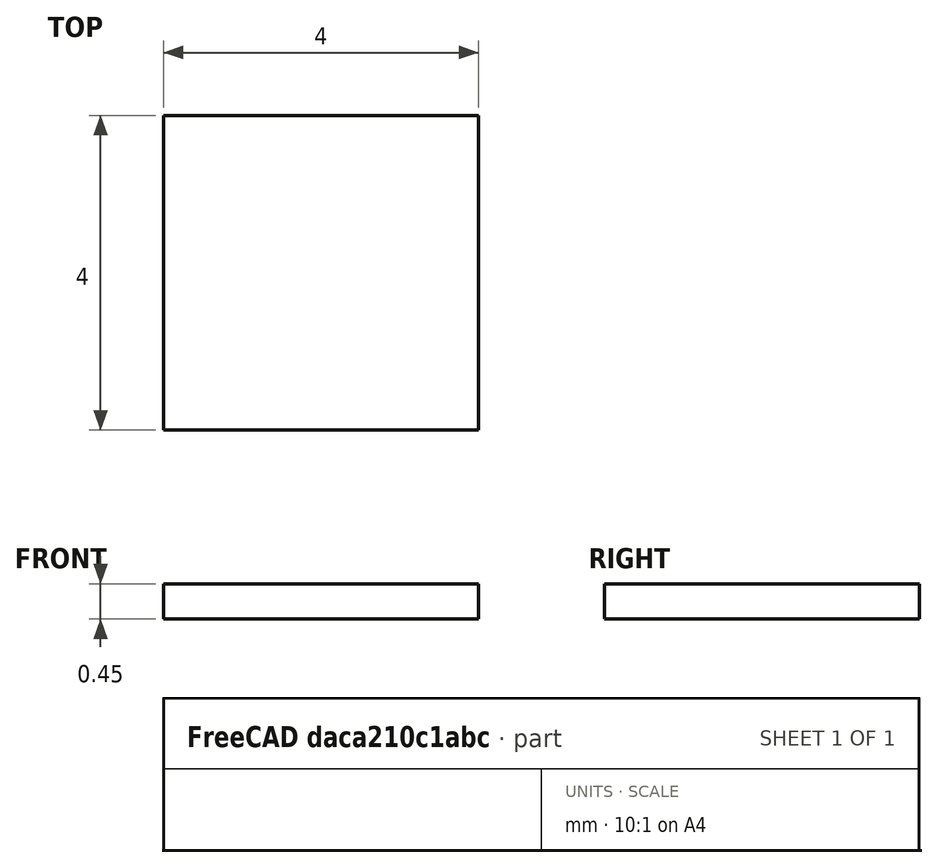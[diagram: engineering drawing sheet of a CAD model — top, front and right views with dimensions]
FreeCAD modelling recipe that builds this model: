
FCSTD DOCUMENT  (FreeCAD 0.20R29410 (Git))
Label: XSON-8 （4x4mm）
License: All rights reserved
LicenseURL: http://en.wikipedia.org/wiki/All_rights_reserved
objects: Sketcher::SketchObject×1, PartDesign::Pad×1, PartDesign::Body×1
note: 4 computed .brp shape members not serialized (recipe doc carries the construction recipe); baked Part::Feature solids carry a one-line shape summary decoded from their .brp

FEATURE [Sketcher::SketchObject] Sketch
  FullyConstrained = true
  MapMode = 5
  Support = -> [XY_Plane]
  sketch-geometry (5):
    g0: LineSegment StartX=-2 StartY=-2 StartZ=0 EndX=-2 EndY=2 EndZ=0
    g1: LineSegment StartX=-2 StartY=2 StartZ=0 EndX=2 EndY=2 EndZ=0
    g2: LineSegment StartX=2 StartY=2 StartZ=0 EndX=2 EndY=-2 EndZ=0
    g3: LineSegment StartX=2 StartY=-2 StartZ=0 EndX=-2 EndY=-2 EndZ=0
    g4: GeomPoint X=1e-16 Y=2e-16 Z=0
  constraints (12):
    c: Coincident(g0,g1)
    c: Coincident(g1,g2)
    c: Coincident(g2,g3)
    c: Coincident(g3,g0)
    c: Horizontal(g1)
    c: Horizontal(g3)
    c: Vertical(g0)
    c: Vertical(g2)
    c: Symmetric(g1,g0,g4)
    c: DistanceX(g1,g1) = 4
    c: DistanceY(g0,g0) = 4
    c: Symmetric(g0,g2,g-1)
FEATURE [PartDesign::Pad] Pad
  Direction = (0,0,1)
  Length = 0.45
  Length2 = 10
  Profile = -> Sketch
  ReferenceAxis = -> Sketch [N_Axis]
  Type = 0
FEATURE [PartDesign::Body] Body
  Group = -> [Sketch,Pad]
  Origin = -> Origin
  Tip = -> Pad
